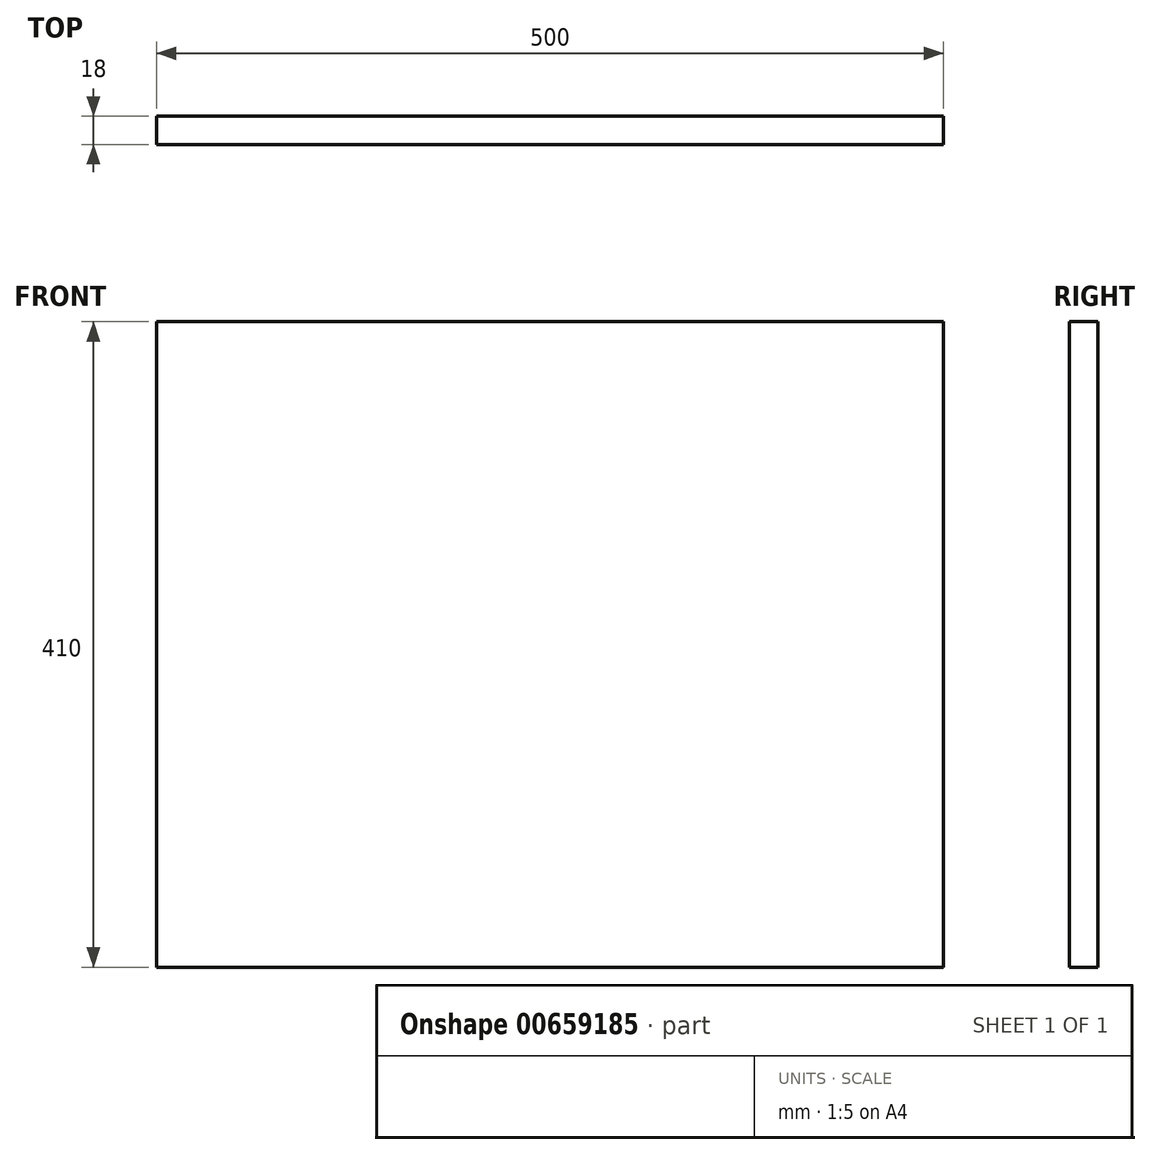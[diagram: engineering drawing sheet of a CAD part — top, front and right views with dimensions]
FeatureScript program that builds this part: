
annotation { "Feature Type Name" : "Feature", "Feature Type Description" : "" }
export const myFeature = defineFeature(function(context is Context, id is Id, definition is map)
    precondition{}
    {
        {
            var Q0;
            Q0=qCreatedBy(makeId("Front.planeOp"),FACE);
            var sketch = newSketch(context, id + "F0", { "sketchPlane" : qUnion([Q0])});
            skLineSegment(sketch, "E0.bottom", {"start": v(-250, -205) * mm, "end": v(250, -205) * mm});
            skLineSegment(sketch, "E0.top", {"start": v(-250, 205) * mm, "end": v(250, 205) * mm});
            skLineSegment(sketch, "E0.left", {"start": v(-250, -205) * mm, "end": v(-250, 205) * mm});
            skLineSegment(sketch, "E0.right", {"start": v(250, -205) * mm, "end": v(250, 205) * mm});
            skPoint(sketch, "E0.middle", {"position": v(0, 0) * mm});
            skSolve(sketch);
        }
        {
            var Q0;
            Q0=makeQuery(id+"F0.imprint","IMPRINT",FACE,{"disambiguationData":[TD([[makeQuery(id+"F0.imprint","IMPRINT",EDGE,{"derivedFrom":sQuery(id+"F0.wireOp",EDGE,"E0.bottom")}),1.0]])]});
            extrude(context, id + "F1", {"entities" : qUnion([Q0]), "endBound" : BoundingType.SYMMETRIC, "depth" : 18 * mm, "offsetDistance" : 25 * mm});
        }
    });
